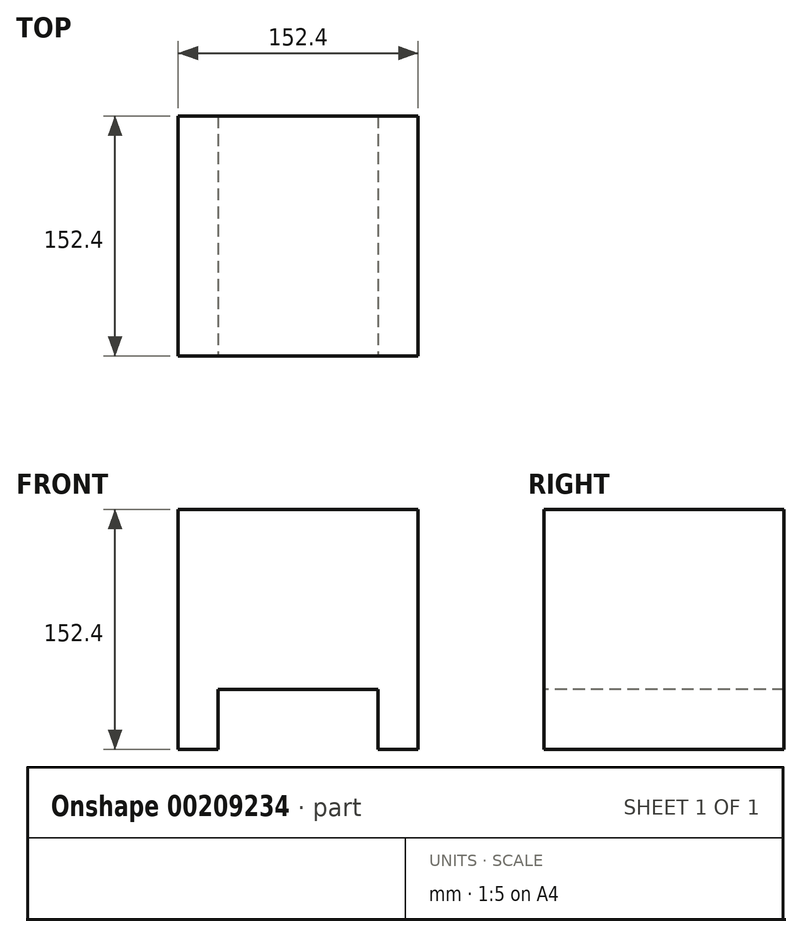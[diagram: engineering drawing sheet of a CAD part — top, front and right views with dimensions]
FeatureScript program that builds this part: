
annotation { "Feature Type Name" : "Feature", "Feature Type Description" : "" }
export const myFeature = defineFeature(function(context is Context, id is Id, definition is map)
    precondition{}
    {
        {
            var Q0;
            Q0=qCreatedBy(makeId("Front.planeOp"),FACE);
            var sketch = newSketch(context, id + "F0", { "sketchPlane" : qUnion([Q0])});
            skLineSegment(sketch, "E0.bottom", {"start": v(0, 0) * mm, "end": v(152.4, 0) * mm});
            skLineSegment(sketch, "E0.top", {"start": v(0, 152.4) * mm, "end": v(152.4, 152.4) * mm});
            skLineSegment(sketch, "E0.left", {"start": v(0, 0) * mm, "end": v(0, 152.4) * mm});
            skLineSegment(sketch, "E0.right", {"start": v(152.4, 0) * mm, "end": v(152.4, 152.4) * mm});
            skSolve(sketch);
        }
        {
            var Q0;
            Q0=makeQuery(id+"F0.imprint","IMPRINT",FACE,{"disambiguationData":[TD([[makeQuery(id+"F0.imprint","IMPRINT",EDGE,{"derivedFrom":sQuery(id+"F0.wireOp",EDGE,"E0.bottom")}),1.0]])]});
            extrude(context, id + "F1", {"entities" : qUnion([Q0]), "oppositeDirection" : true, "depth" : 152.4 * mm});
        }
        {
            var Q0;
            Q0=makeQuery(id+"F1.opExtrude","CAP_FACE",FACE,{"disambiguationData":[OSD([sQuery(id+"F0.wireOp",EDGE,"E0.bottom"),sQuery(id+"F0.wireOp",EDGE,"E0.top"),sQuery(id+"F0.wireOp",EDGE,"E0.left"),sQuery(id+"F0.wireOp",EDGE,"E0.right")])],"isStart":true});
            var sketch = newSketch(context, id + "F2", { "sketchPlane" : qUnion([Q0])});
            skLineSegment(sketch, "E1.bottom", {"start": v(25.4, 0) * mm, "end": v(127, 0) * mm});
            skLineSegment(sketch, "E1.top", {"start": v(25.4, 38.1) * mm, "end": v(127, 38.1) * mm});
            skLineSegment(sketch, "E1.left", {"start": v(25.4, 0) * mm, "end": v(25.4, 38.1) * mm});
            skLineSegment(sketch, "E1.right", {"start": v(127, 0) * mm, "end": v(127, 38.1) * mm});
            skSolve(sketch);
        }
        {
            var Q0;
            Q0=makeQuery(id+"F2.imprint","IMPRINT",FACE,{"disambiguationData":[TD([[makeQuery(id+"F2.imprint","IMPRINT",EDGE,{"derivedFrom":sQuery(id+"F2.wireOp",EDGE,"E1.bottom")}),1.0]])]});
            extrude(context, id + "F3", {"entities" : qUnion([Q0]), "operationType" : NewBodyOperationType.REMOVE, "endBound" : BoundingType.THROUGH_ALL, "oppositeDirection" : true, "depth" : 37.6 * mm});
        }
    });
